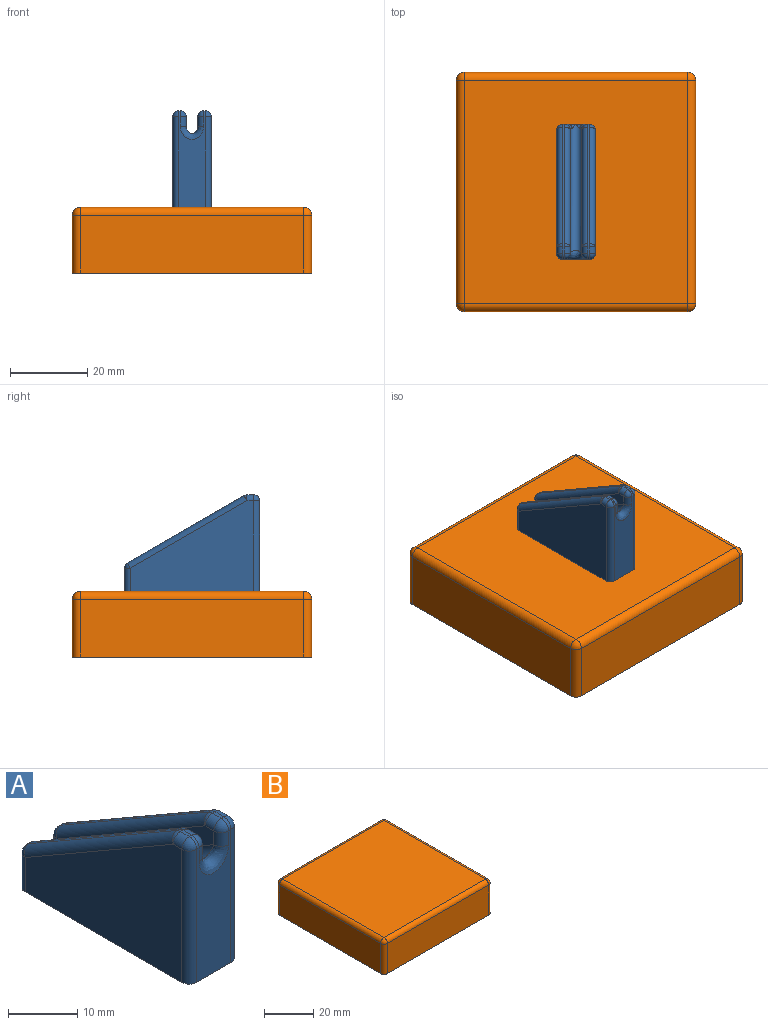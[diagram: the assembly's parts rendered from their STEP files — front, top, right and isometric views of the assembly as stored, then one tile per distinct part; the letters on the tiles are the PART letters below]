
ASSEMBLY  parts=2 mates=1
PART A: 52 faces, bbox 10x35.8x25 mm
  f0: plane 6.06x1.52mm, normal (0,1,0), area 3.8mm2, adj f8,f21,f25,f28,f29
  f1: plane 1.8x0.5mm, normal (0,0,1), area 0.9mm2, adj f13,f41,f46,f47
  f2: plane 30.2x17.44mm, normal (0,0.5,0.87), area 17.4mm2, adj f13,f15,f16,f18
  f3: plane 6.06x1.52mm, normal (0,1,0), area 3.8mm2, adj f8,f14,f18,f32,f33
  f4: plane 32x23.5mm, normal (-1,0,0), area 488.7mm2, adj f8,f20,f21,f22,f36
  f5: plane 23.5x7mm, normal (0,-1,0), area 133.6mm2, adj f8,f12,f20,f42,f47,f48,f50,f51
  f6: plane 32x23.5mm, normal (1,0,0), area 488.7mm2, adj f8,f12,f14,f15,f41
  f7: plane 1.8x0.5mm, normal (0,0,1), area 0.9mm2, adj f24,f36,f42,f43
  f8: plane 35x10mm, normal (0,0,-1), area 348.1mm2, adj f0,f3,f4,f5,f6,f12,f14,f20
  f9: plane 30.2x17.44mm, normal (0,0.5,0.87), area 17.4mm2, adj f22,f24,f25,f26
  f10: plane 32x20.9mm, normal (1,0,0), area 109.9mm2, adj f19,f26,f29,f43,f48
  f11: plane 32x20.9mm, normal (-1,0,0), area 109.9mm2, adj f16,f19,f33,f46,f51
  f12: cylinder r=1.5mm len=23.5mm, axis (0,0,1), area 55.4mm2, adj f5,f6,f8,f44
  f13: cylinder r=1.5mm len=0.75mm, axis (-1,0,0), area 0.4mm2, adj f1,f2,f38,f40
  f14: cylinder r=1.5mm len=6.06mm, axis (0,0,-1), area 14.3mm2, adj f3,f6,f8,f17
  f15: cylinder r=1.5mm len=30.95mm, axis (0,-0.87,0.5), area 82.2mm2, adj f2,f6,f17,f38
  f16: cylinder r=1.5mm len=30.95mm, axis (0,0.87,-0.5), area 82.2mm2, adj f2,f11,f34,f40
  f17: sphere r=1.5mm, area 2.4mm2, adj f14,f15,f18
  f18: cylinder r=1.5mm len=1.3mm, axis (-1,0,0), area 0.8mm2, adj f2,f3,f17,f34
  f19: cylinder r=1.5mm len=35mm, axis (0,0.87,-0.5), area 174.8mm2, adj f10,f11,f27,f28,f31,f32,f50
  f20: cylinder r=1.5mm len=23.5mm, axis (0,0,-1), area 55.4mm2, adj f4,f5,f8,f39
  f21: cylinder r=1.5mm len=6.06mm, axis (0,0,1), area 14.3mm2, adj f0,f4,f8,f23
  f22: cylinder r=1.5mm len=30.95mm, axis (0,0.87,-0.5), area 82.2mm2, adj f4,f9,f23,f35
  f23: sphere r=1.5mm, area 2.4mm2, adj f21,f22,f25
  f24: cylinder r=1.5mm len=0.75mm, axis (-1,0,0), area 0.4mm2, adj f7,f9,f35,f37
  f25: cylinder r=1.5mm len=1.3mm, axis (-1,0,0), area 0.8mm2, adj f0,f9,f23,f30
  f26: cylinder r=1.5mm len=30.95mm, axis (0,-0.87,0.5), area 82.2mm2, adj f9,f10,f30,f37
  f27: bspline ~2.2x1.12mm, area 1.1mm2, adj f8,f19,f28
  f28: bspline ~2.6x2.01mm, area 4.5mm2, adj f0,f19,f27,f29
  f29: cylinder r=1.5mm len=3.46mm, axis (0,0,-1), area 8.2mm2, adj f0,f10,f28,f30
  f30: sphere r=1.5mm, area 2.4mm2, adj f25,f26,f29
  f31: bspline ~2.2x1.12mm, area 1.2mm2, adj f8,f19,f32
  f32: bspline ~2.6x2.01mm, area 4.5mm2, adj f3,f19,f31,f33
  f33: cylinder r=1.5mm len=3.46mm, axis (0,0,1), area 8.2mm2, adj f3,f11,f32,f34
  f34: sphere r=1.5mm, area 2.4mm2, adj f16,f18,f33
  f35: sphere r=1.5mm, area 1.2mm2, adj f22,f24,f36
  f36: cylinder r=1.5mm len=1.8mm, axis (0,1,0), area 4.2mm2, adj f4,f7,f35,f39
  f37: sphere r=1.5mm, area 1.2mm2, adj f24,f26,f43
  f38: sphere r=1.5mm, area 1.2mm2, adj f13,f15,f41
  f39: sphere r=1.5mm, area 3.5mm2, adj f20,f36,f42
  f40: sphere r=1.5mm, area 1.2mm2, adj f13,f16,f46
  f41: cylinder r=1.5mm len=1.8mm, axis (0,1,0), area 4.2mm2, adj f1,f6,f38,f44
  f42: cylinder r=1.5mm len=1.5mm, axis (-1,0,0), area 1.2mm2, adj f5,f7,f39,f45
  f43: cylinder r=1.5mm len=1.8mm, axis (0,-1,0), area 4.2mm2, adj f7,f10,f37,f45
  f44: sphere r=1.5mm, area 3.5mm2, adj f12,f41,f47
  f45: sphere r=1.5mm, area 3.5mm2, adj f42,f43,f48
  f46: cylinder r=1.5mm len=1.8mm, axis (0,1,0), area 4.2mm2, adj f1,f11,f40,f49
  f47: cylinder r=1.5mm len=1.5mm, axis (-1,0,0), area 1.2mm2, adj f1,f5,f44,f49
  f48: cylinder r=1.5mm len=2.43mm, axis (0,0,1), area 5.7mm2, adj f5,f10,f45,f50
  f49: sphere r=1.5mm, area 3.5mm2, adj f46,f47,f51
  f50: bspline ~6x3.46mm, area 19.4mm2, adj f5,f19,f48,f51
  f51: cylinder r=1.5mm len=2.43mm, axis (0,0,-1), area 5.7mm2, adj f5,f11,f49,f50
PART B: 23 faces, bbox 62x62x17 mm
  f0: plane 62x62mm, normal (0,0,-1), area 240.6mm2, adj f1,f2,f3,f4,f6,f7,f8,f9
  f1: plane 58x15mm, normal (0,1,0), area 870mm2, adj f0,f13,f19,f22
  f2: plane 58x15mm, normal (-1,0,0), area 870mm2, adj f0,f16,f20,f22
  f3: plane 58x15mm, normal (0,-1,0), area 870mm2, adj f0,f11,f15,f16
  f4: plane 58x15mm, normal (1,0,0), area 870mm2, adj f0,f11,f13,f14
  f5: plane 58x58mm, normal (0,0,1), area 3364mm2, adj f14,f15,f19,f20
  f6: plane 60x15mm, normal (-1,0,0), area 900mm2, adj f0,f7,f9,f10
  f7: plane 60x15mm, normal (0,1,0), area 900mm2, adj f0,f6,f8,f10
  f8: plane 60x15mm, normal (1,0,0), area 900mm2, adj f0,f7,f9,f10
  f9: plane 60x15mm, normal (0,-1,0), area 900mm2, adj f0,f6,f8,f10
  f10: plane 60x60mm, normal (0,0,-1), area 3600mm2, adj f6,f7,f8,f9
  f11: cylinder r=2mm len=15mm, axis (0,0,1), area 47.1mm2, adj f0,f3,f4,f12
  f12: sphere r=2mm, area 6.3mm2, adj f11,f14,f15
  f13: cylinder r=2mm len=15mm, axis (0,0,-1), area 47.1mm2, adj f0,f1,f4,f17
  f14: cylinder r=2mm len=58mm, axis (0,-1,0), area 182.2mm2, adj f4,f5,f12,f17
  f15: cylinder r=2mm len=58mm, axis (-1,0,0), area 182.2mm2, adj f3,f5,f12,f18
  f16: cylinder r=2mm len=15mm, axis (0,0,-1), area 47.1mm2, adj f0,f2,f3,f18
  f17: sphere r=2mm, area 6.3mm2, adj f13,f14,f19
  f18: sphere r=2mm, area 6.3mm2, adj f15,f16,f20
  f19: cylinder r=2mm len=58mm, axis (1,0,0), area 182.2mm2, adj f1,f5,f17,f21
  f20: cylinder r=2mm len=58mm, axis (0,1,0), area 182.2mm2, adj f2,f5,f18,f21
  f21: sphere r=2mm, area 6.3mm2, adj f19,f20,f22
  f22: cylinder r=2mm len=15mm, axis (0,0,1), area 47.1mm2, adj f0,f1,f2,f21
PLACE A t=(0.42,-35.17,15.8)mm
PLACE B t=(-13.83,-26.81,-1.2)mm
MATE fastened A.f8 <-> B.f5  axis (0,0,-1) through (-14.74,-25.69,15.8)mm
